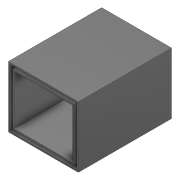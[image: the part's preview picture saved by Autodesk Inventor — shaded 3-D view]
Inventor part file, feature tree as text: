
AUTODESK INVENTOR PART (.ipt)
format: ipt  version: 2020 (Build 240168000, 168)  size: 170,496 bytes
history: native  units: mm
features: extrude x7, sketch x7
ambient origin geometry x8: Origin, YZ Plane, XZ Plane, XY Plane, X Axis, Y Axis, Z Axis, Center Point
bodies: Volumenkörper1 (feature_tree)
feature tree (14):
  extrude  "Extrusion1"  Depth=100.0mm
  extrude  "Extrusion2"  Depth=10.0mm
  extrude  "Extrusion3"  Depth=10.0mm
  extrude  "Extrusion4"  Depth=10.0mm TaperAngle=0.0deg
  extrude  "Extrusion5"  Depth=10.0mm
  extrude  "Extrusion6"  Depth=30.0mm
  extrude  "Extrusion7"  Depth=10.0mm
  sketch  "Skizze1"  dims[d0=85.0mm d1=100.0mm]
  sketch  "Skizze2"  dims[d2=10.0mm d3=10.0mm]
  sketch  "Skizze3"  dims[d4=10.0mm d5=10.0mm]
  sketch  "Skizze4"  dims[d6=160.0mm d7=0.0mm d8=10.0mm d9=0.0mm]
  sketch  "Skizze5"  dims[d10=10.0mm d11=10.0mm]
  sketch  "Skizze6"  dims[d12=10.0mm d13=30.0mm]
  sketch  "Skizze7"  dims[d14=10.0mm d15=0.0mm d16=10.0mm d17=10.0mm d18=120.0mm d19=0.0mm d20=2.4mm d21=2.4mm d22=2.4mm d23=2.4mm d24=2.4mm d25=2.4mm d26=2.4mm d27=2.4mm d28=7.5mm d29=0.0mm d30=10.0mm d31=0.0mm d32=10.0mm d33=10.0mm d34=10.0mm d35=30.0mm d36=10.0mm d37=0.0mm]
